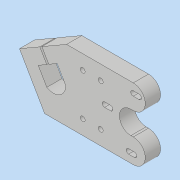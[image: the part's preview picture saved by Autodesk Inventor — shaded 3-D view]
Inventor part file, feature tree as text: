
AUTODESK INVENTOR PART (.ipt)
format: ipt  version: 2017 (Build 210142000, 142)  size: 204,288 bytes
history: native  units: in
note: dims shown in document units (in); Inventor stores cm internally (conversion verified against a paired STEP export)
features: sketch x3, extrude x3, fillet x2, plane x1
ambient origin geometry x8: Origin, YZ Plane, XZ Plane, XY Plane, X Axis, Y Axis, Z Axis, Center Point
bodies: Solid8 (feature_tree)
feature tree (9):
  sketch  "sketch_plate"  dims[d8=0.72in d9=0.56in]
  extrude  "Extrusion10"  Depth=0.72in
  sketch  "sketch_clampscrew"  dims[d10=0.41in d13=0.45in]
  extrude  "extr_clampscrew"  Depth=0.45in
  plane  "Work Plane1"
  sketch  "sketch_clampscrewhead"  dims[d14=0.45in d15=0.0787in d17=2.3228in d18=0.313in d19=0.36in d20=0.365in d21=30.0deg d22=0.3287in d23=2.5606in d25=0.159in d26=0.159in d27=0.159in d28=0.159in d32=0.75in d33=0.1575in d34=0.1575in d35=0.1575in d36=0.1575in d38=1.2205in d39=1.2205in d40=1.2205in d41=1.2205in d42=0.5906in d43=1.378in d44=1.378in d49=0.1575in d50=0.1575in d51=0.1575in d52=0.1575in d53=0.1969in d54=2.3228in d55=2.6406in d56=0.75in d57=0.1969in d58=0.1969in d59=0.1969in d60=0.1575in d61=0.1575in d62=0.1575in d63=0.1575in d68=0.0344in d69=0.0344in d70=1.2205in d71=1.2205in d72=1.2205in d73=1.2205in d87=0.159in d88=0.5in d89=0.0in d90=0.5in d91=0.0in d92=2.1864in d93=0.1575in d94=0.1575in d95=0.9843in d96=0.5in d97=0.0in]
  extrude  "extr_clampscrewhead"  Depth=0.0787in
  fillet  "Fillet1"  Radius=2.3228in
  fillet  "Fillet2"  Radius=0.313in
